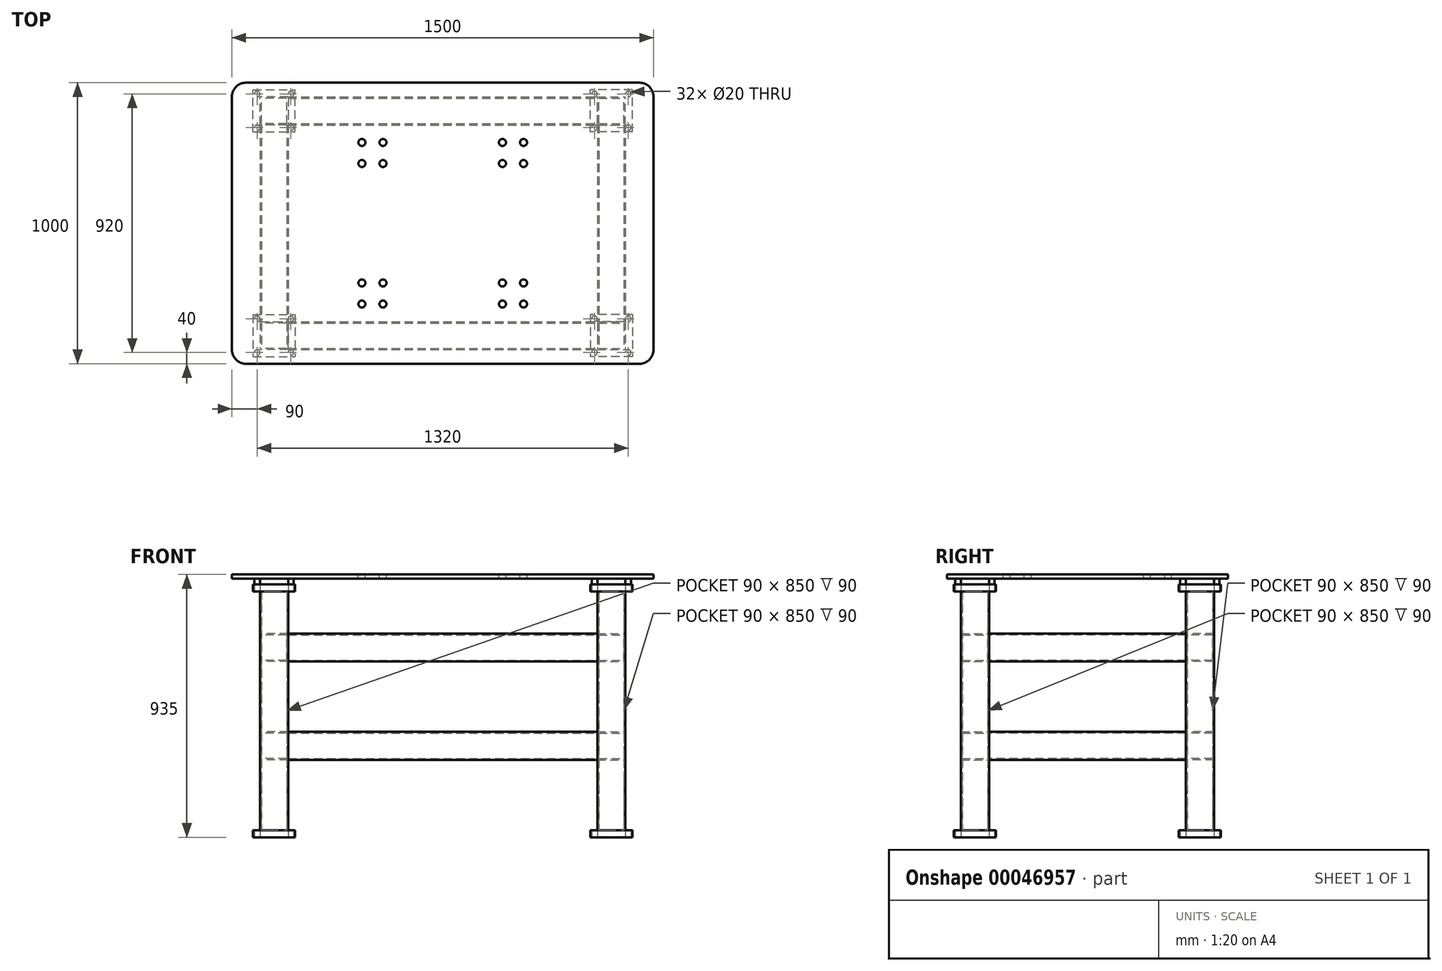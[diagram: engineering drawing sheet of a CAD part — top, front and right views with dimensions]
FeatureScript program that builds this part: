
annotation { "Feature Type Name" : "Feature", "Feature Type Description" : "" }
export const myFeature = defineFeature(function(context is Context, id is Id, definition is map)
    precondition{}
    {
        {
            var Q0;
            Q0=qCreatedBy(makeId("Top.planeOp"),FACE);
            var sketch = newSketch(context, id + "F0", { "sketchPlane" : qUnion([Q0])});
            skLineSegment(sketch, "E0.rect.bottom", {"start": v(-600, -400) * mm, "end": v(600, -400) * mm, "construction": true});
            skLineSegment(sketch, "E0.rect.top", {"start": v(-600, 400) * mm, "end": v(600, 400) * mm, "construction": true});
            skLineSegment(sketch, "E0.rect.left", {"start": v(-600, -400) * mm, "end": v(-600, 400) * mm, "construction": true});
            skLineSegment(sketch, "E0.rect.right", {"start": v(600, -400) * mm, "end": v(600, 400) * mm, "construction": true});
            skPoint(sketch, "E0.rect.middle", {"position": v(0, 0) * mm});
            skLineSegment(sketch, "E1.rect.bottom", {"start": v(-675, 325) * mm, "end": v(-525, 325) * mm});
            skLineSegment(sketch, "E1.rect.top", {"start": v(-675, 475) * mm, "end": v(-525, 475) * mm});
            skLineSegment(sketch, "E1.rect.left", {"start": v(-675, 325) * mm, "end": v(-675, 475) * mm});
            skLineSegment(sketch, "E1.rect.right", {"start": v(-525, 325) * mm, "end": v(-525, 475) * mm});
            skPoint(sketch, "E1.rect.middle", {"position": v(-600, 400) * mm});
            skLineSegment(sketch, "E2.rect.bottom", {"start": v(-660, 340) * mm, "end": v(-540, 340) * mm, "construction": true});
            skLineSegment(sketch, "E2.rect.top", {"start": v(-660, 460) * mm, "end": v(-540, 460) * mm, "construction": true});
            skLineSegment(sketch, "E2.rect.left", {"start": v(-660, 340) * mm, "end": v(-660, 460) * mm, "construction": true});
            skLineSegment(sketch, "E2.rect.right", {"start": v(-540, 340) * mm, "end": v(-540, 460) * mm, "construction": true});
            skCircle(sketch, "E3", {"center": v(-660, 460) * mm, "radius": 10 * mm});
            skCircle(sketch, "E4", {"center": v(-540, 460) * mm, "radius": 10 * mm});
            skCircle(sketch, "E5", {"center": v(-660, 340) * mm, "radius": 10 * mm});
            skCircle(sketch, "E6", {"center": v(-540, 340) * mm, "radius": 10 * mm});
            skCircle(sketch, "E7.MirrorC", {"center": v(540, 340) * mm, "radius": 10 * mm});
            skCircle(sketch, "E8.MirrorC", {"center": v(660, 460) * mm, "radius": 10 * mm});
            skCircle(sketch, "E9.MirrorC", {"center": v(660, 340) * mm, "radius": 10 * mm});
            skCircle(sketch, "E10.MirrorC", {"center": v(540, 460) * mm, "radius": 10 * mm});
            skPoint(sketch, "E11.MirrorP", {"position": v(600, 400) * mm});
            skLineSegment(sketch, "E12.MirrorCS", {"start": v(540, 340) * mm, "end": v(540, 460) * mm, "construction": true});
            skLineSegment(sketch, "E13.MirrorCS", {"start": v(660, 340) * mm, "end": v(660, 460) * mm, "construction": true});
            skLineSegment(sketch, "E14.MirrorCS", {"start": v(660, 460) * mm, "end": v(540, 460) * mm, "construction": true});
            skLineSegment(sketch, "E15.MirrorCS", {"start": v(675, 325) * mm, "end": v(525, 325) * mm});
            skLineSegment(sketch, "E16.MirrorCS", {"start": v(675, 475) * mm, "end": v(525, 475) * mm});
            skLineSegment(sketch, "E17.MirrorCS", {"start": v(675, 325) * mm, "end": v(675, 475) * mm});
            skLineSegment(sketch, "E18.MirrorCS", {"start": v(525, 325) * mm, "end": v(525, 475) * mm});
            skLineSegment(sketch, "E19.MirrorCS", {"start": v(660, 340) * mm, "end": v(540, 340) * mm, "construction": true});
            skCircle(sketch, "E20.MirrorC", {"center": v(540, -340) * mm, "radius": 10 * mm});
            skCircle(sketch, "E21.MirrorC", {"center": v(660, -340) * mm, "radius": 10 * mm});
            skCircle(sketch, "E22.MirrorC", {"center": v(-660, -460) * mm, "radius": 10 * mm});
            skCircle(sketch, "E23.MirrorC", {"center": v(-540, -340) * mm, "radius": 10 * mm});
            skCircle(sketch, "E24.MirrorC", {"center": v(-660, -340) * mm, "radius": 10 * mm});
            skCircle(sketch, "E25.MirrorC", {"center": v(-540, -460) * mm, "radius": 10 * mm});
            skCircle(sketch, "E26.MirrorC", {"center": v(660, -460) * mm, "radius": 10 * mm});
            skCircle(sketch, "E27.MirrorC", {"center": v(540, -460) * mm, "radius": 10 * mm});
            skPoint(sketch, "E28.MirrorP", {"position": v(600, -400) * mm});
            skPoint(sketch, "E29.MirrorP", {"position": v(-600, -400) * mm});
            skLineSegment(sketch, "E30.MirrorCS", {"start": v(540, -340) * mm, "end": v(540, -460) * mm, "construction": true});
            skLineSegment(sketch, "E31.MirrorCS", {"start": v(660, -460) * mm, "end": v(540, -460) * mm, "construction": true});
            skLineSegment(sketch, "E32.MirrorCS", {"start": v(675, -325) * mm, "end": v(525, -325) * mm});
            skLineSegment(sketch, "E33.MirrorCS", {"start": v(675, -325) * mm, "end": v(675, -475) * mm});
            skLineSegment(sketch, "E34.MirrorCS", {"start": v(660, -340) * mm, "end": v(540, -340) * mm, "construction": true});
            skLineSegment(sketch, "E35.MirrorCS", {"start": v(-540, -340) * mm, "end": v(-540, -460) * mm, "construction": true});
            skLineSegment(sketch, "E36.MirrorCS", {"start": v(-660, -340) * mm, "end": v(-660, -460) * mm, "construction": true});
            skLineSegment(sketch, "E37.MirrorCS", {"start": v(-660, -460) * mm, "end": v(-540, -460) * mm, "construction": true});
            skLineSegment(sketch, "E38.MirrorCS", {"start": v(-660, -340) * mm, "end": v(-540, -340) * mm, "construction": true});
            skLineSegment(sketch, "E39.MirrorCS", {"start": v(-525, -325) * mm, "end": v(-525, -475) * mm});
            skLineSegment(sketch, "E40.MirrorCS", {"start": v(-675, -325) * mm, "end": v(-675, -475) * mm});
            skLineSegment(sketch, "E41.MirrorCS", {"start": v(-675, -475) * mm, "end": v(-525, -475) * mm});
            skLineSegment(sketch, "E42.MirrorCS", {"start": v(-600, -400) * mm, "end": v(600, -400) * mm});
            skLineSegment(sketch, "E43.MirrorCS", {"start": v(525, -325) * mm, "end": v(525, -475) * mm});
            skLineSegment(sketch, "E44.MirrorCS", {"start": v(-675, -325) * mm, "end": v(-525, -325) * mm});
            skLineSegment(sketch, "E45.MirrorCS", {"start": v(660, -340) * mm, "end": v(660, -460) * mm, "construction": true});
            skLineSegment(sketch, "E46.MirrorCS", {"start": v(675, -475) * mm, "end": v(525, -475) * mm});
            skSolve(sketch);
        }
        {
            var Q0;
            Q0=qSketchRegion(id+"F0",true);
            extrude(context, id + "F1", {"entities" : qUnion([Q0]), "depth" : 25 * mm});
        }
        {
            var Q0;
            Q0=makeQuery(id+"F1.opExtrude","CAP_FACE",FACE,{"disambiguationData":[OSD([sQuery(id+"F0.wireOp",EDGE,"E1.rect.bottom"),sQuery(id+"F0.wireOp",EDGE,"E1.rect.top"),sQuery(id+"F0.wireOp",EDGE,"E1.rect.left"),sQuery(id+"F0.wireOp",EDGE,"E1.rect.right"),sQuery(id+"F0.wireOp",EDGE,"E3"),sQuery(id+"F0.wireOp",EDGE,"E4"),sQuery(id+"F0.wireOp",EDGE,"E5"),sQuery(id+"F0.wireOp",EDGE,"E6")])],"isStart":false});
            var sketch = newSketch(context, id + "F2", { "sketchPlane" : qUnion([Q0])});
            skLineSegment(sketch, "E47.rect.bottom", {"start": v(-550, 350) * mm, "end": v(-650, 350) * mm});
            skLineSegment(sketch, "E47.rect.top", {"start": v(-550, 450) * mm, "end": v(-650, 450) * mm});
            skLineSegment(sketch, "E47.rect.left", {"start": v(-550, 350) * mm, "end": v(-550, 450) * mm});
            skLineSegment(sketch, "E47.rect.right", {"start": v(-650, 350) * mm, "end": v(-650, 450) * mm});
            skPoint(sketch, "E47.rect.middle", {"position": v(-600, 400) * mm});
            skPoint(sketch, "E47.rect.middle.positionSnap0", {"position": v(-675, 400) * mm});
            skPoint(sketch, "E47.rect.centerSnap0", {"position": v(-675, 400) * mm});
            skLineSegment(sketch, "E48.rect.bottom", {"start": v(-555, 355) * mm, "end": v(-645, 355) * mm});
            skLineSegment(sketch, "E48.rect.top", {"start": v(-555, 445) * mm, "end": v(-645, 445) * mm});
            skLineSegment(sketch, "E48.rect.left", {"start": v(-555, 355) * mm, "end": v(-555, 445) * mm});
            skLineSegment(sketch, "E48.rect.right", {"start": v(-645, 355) * mm, "end": v(-645, 445) * mm});
            skPoint(sketch, "E49.MirrorP", {"position": v(600, 400) * mm});
            skPoint(sketch, "E50.MirrorP", {"position": v(675, 400) * mm});
            skLineSegment(sketch, "E51.MirrorCS", {"start": v(645, 355) * mm, "end": v(645, 445) * mm});
            skLineSegment(sketch, "E52.MirrorCS", {"start": v(555, 355) * mm, "end": v(555, 445) * mm});
            skLineSegment(sketch, "E53.MirrorCS", {"start": v(555, 445) * mm, "end": v(645, 445) * mm});
            skLineSegment(sketch, "E54.MirrorCS", {"start": v(555, 355) * mm, "end": v(645, 355) * mm});
            skLineSegment(sketch, "E55.MirrorCS", {"start": v(650, 350) * mm, "end": v(650, 450) * mm});
            skLineSegment(sketch, "E56.MirrorCS", {"start": v(550, 350) * mm, "end": v(650, 350) * mm});
            skLineSegment(sketch, "E57.MirrorCS", {"start": v(550, 350) * mm, "end": v(550, 450) * mm});
            skLineSegment(sketch, "E58.MirrorCS", {"start": v(550, 450) * mm, "end": v(650, 450) * mm});
            skLineSegment(sketch, "E59.MirrorCS", {"start": v(650, -350) * mm, "end": v(650, -450) * mm});
            skPoint(sketch, "E60.MirrorP", {"position": v(-675, -400) * mm});
            skPoint(sketch, "E61.MirrorP", {"position": v(600, -400) * mm});
            skPoint(sketch, "E62.MirrorP", {"position": v(-600, -400) * mm});
            skPoint(sketch, "E63.MirrorP", {"position": v(675, -400) * mm});
            skLineSegment(sketch, "E64.MirrorCS", {"start": v(-555, -355) * mm, "end": v(-555, -445) * mm});
            skLineSegment(sketch, "E65.MirrorCS", {"start": v(-555, -445) * mm, "end": v(-645, -445) * mm});
            skLineSegment(sketch, "E66.MirrorCS", {"start": v(-555, -355) * mm, "end": v(-645, -355) * mm});
            skLineSegment(sketch, "E67.MirrorCS", {"start": v(-650, -350) * mm, "end": v(-650, -450) * mm});
            skLineSegment(sketch, "E68.MirrorCS", {"start": v(-550, -350) * mm, "end": v(-550, -450) * mm});
            skLineSegment(sketch, "E69.MirrorCS", {"start": v(-550, -450) * mm, "end": v(-650, -450) * mm});
            skLineSegment(sketch, "E70.MirrorCS", {"start": v(-550, -350) * mm, "end": v(-650, -350) * mm});
            skLineSegment(sketch, "E71.MirrorCS", {"start": v(550, -450) * mm, "end": v(650, -450) * mm});
            skLineSegment(sketch, "E72.MirrorCS", {"start": v(550, -350) * mm, "end": v(550, -450) * mm});
            skLineSegment(sketch, "E73.MirrorCS", {"start": v(550, -350) * mm, "end": v(650, -350) * mm});
            skLineSegment(sketch, "E74.MirrorCS", {"start": v(-645, -355) * mm, "end": v(-645, -445) * mm});
            skLineSegment(sketch, "E75.MirrorCS", {"start": v(645, -355) * mm, "end": v(645, -445) * mm});
            skLineSegment(sketch, "E76.MirrorCS", {"start": v(555, -355) * mm, "end": v(555, -445) * mm});
            skLineSegment(sketch, "E77.MirrorCS", {"start": v(555, -355) * mm, "end": v(645, -355) * mm});
            skLineSegment(sketch, "E78.MirrorCS", {"start": v(555, -445) * mm, "end": v(645, -445) * mm});
            skSolve(sketch);
        }
        {
            var Q0;
            Q0=qSketchRegion(id+"F2",true);
            extrude(context, id + "F3", {"entities" : qUnion([Q0]), "operationType" : NewBodyOperationType.ADD, "depth" : 850 * mm});
        }
        {
            var Q0;
            Q0=makeQuery(id+"F3.opExtrude","CAP_FACE",FACE,{"disambiguationData":[OSD([sQuery(id+"F2.wireOp",EDGE,"E47.rect.bottom"),sQuery(id+"F2.wireOp",EDGE,"E47.rect.top"),sQuery(id+"F2.wireOp",EDGE,"E47.rect.left"),sQuery(id+"F2.wireOp",EDGE,"E47.rect.right"),sQuery(id+"F2.wireOp",EDGE,"E48.rect.bottom"),sQuery(id+"F2.wireOp",EDGE,"E48.rect.top"),sQuery(id+"F2.wireOp",EDGE,"E48.rect.left"),sQuery(id+"F2.wireOp",EDGE,"E48.rect.right")])],"isStart":false});
            var sketch = newSketch(context, id + "F4", { "sketchPlane" : qUnion([Q0])});
            skLineSegment(sketch, "E79.rect.bottom", {"start": v(-600, -400) * mm, "end": v(600, -400) * mm, "construction": true});
            skLineSegment(sketch, "E79.rect.top", {"start": v(-600, 400) * mm, "end": v(600, 400) * mm, "construction": true});
            skLineSegment(sketch, "E79.rect.left", {"start": v(-600, -400) * mm, "end": v(-600, 400) * mm, "construction": true});
            skLineSegment(sketch, "E79.rect.right", {"start": v(600, -400) * mm, "end": v(600, 400) * mm, "construction": true});
            skLineSegment(sketch, "E80.rect.bottom", {"start": v(-675, 325) * mm, "end": v(-525, 325) * mm});
            skLineSegment(sketch, "E80.rect.top", {"start": v(-675, 475) * mm, "end": v(-525, 475) * mm});
            skLineSegment(sketch, "E80.rect.left", {"start": v(-675, 325) * mm, "end": v(-675, 475) * mm});
            skLineSegment(sketch, "E80.rect.right", {"start": v(-525, 325) * mm, "end": v(-525, 475) * mm});
            skPoint(sketch, "E80.rect.middle", {"position": v(-600, 400) * mm});
            skLineSegment(sketch, "E81.rect.bottom", {"start": v(-660, 340) * mm, "end": v(-540, 340) * mm, "construction": true});
            skLineSegment(sketch, "E81.rect.top", {"start": v(-660, 460) * mm, "end": v(-540, 460) * mm, "construction": true});
            skLineSegment(sketch, "E81.rect.left", {"start": v(-660, 340) * mm, "end": v(-660, 460) * mm, "construction": true});
            skLineSegment(sketch, "E81.rect.right", {"start": v(-540, 340) * mm, "end": v(-540, 460) * mm, "construction": true});
            skCircle(sketch, "E82", {"center": v(-660, 460) * mm, "radius": 10 * mm});
            skCircle(sketch, "E83", {"center": v(-540, 460) * mm, "radius": 10 * mm});
            skCircle(sketch, "E84", {"center": v(-660, 340) * mm, "radius": 10 * mm});
            skCircle(sketch, "E85", {"center": v(-540, 340) * mm, "radius": 10 * mm});
            skPoint(sketch, "E86.MirrorP", {"position": v(600, 400) * mm});
            skPoint(sketch, "E87.MirrorP", {"position": v(-1214.7, -400) * mm});
            skLineSegment(sketch, "E88.MirrorCS", {"start": v(-1214.7, -400) * mm, "end": v(-14.7, -400) * mm});
            skCircle(sketch, "E89.MirrorC", {"center": v(540, 340) * mm, "radius": 10 * mm});
            skCircle(sketch, "E90.MirrorC", {"center": v(660, 460) * mm, "radius": 10 * mm});
            skCircle(sketch, "E91.MirrorC", {"center": v(660, 340) * mm, "radius": 10 * mm});
            skCircle(sketch, "E92.MirrorC", {"center": v(540, 460) * mm, "radius": 10 * mm});
            skLineSegment(sketch, "E93.MirrorCS", {"start": v(660, 340) * mm, "end": v(540, 340) * mm, "construction": true});
            skLineSegment(sketch, "E94.MirrorCS", {"start": v(525, 325) * mm, "end": v(525, 475) * mm});
            skLineSegment(sketch, "E95.MirrorCS", {"start": v(675, 325) * mm, "end": v(675, 475) * mm});
            skLineSegment(sketch, "E96.MirrorCS", {"start": v(540, 340) * mm, "end": v(540, 460) * mm, "construction": true});
            skLineSegment(sketch, "E97.MirrorCS", {"start": v(675, 475) * mm, "end": v(525, 475) * mm});
            skLineSegment(sketch, "E98.MirrorCS", {"start": v(660, 340) * mm, "end": v(660, 460) * mm, "construction": true});
            skLineSegment(sketch, "E99.MirrorCS", {"start": v(660, 460) * mm, "end": v(540, 460) * mm, "construction": true});
            skLineSegment(sketch, "E100.MirrorCS", {"start": v(675, 325) * mm, "end": v(525, 325) * mm});
            skCircle(sketch, "E101.MirrorC", {"center": v(-660, -460) * mm, "radius": 10 * mm});
            skPoint(sketch, "E102.MirrorP", {"position": v(600, -400) * mm});
            skCircle(sketch, "E103.MirrorC", {"center": v(660, -460) * mm, "radius": 10 * mm});
            skCircle(sketch, "E104.MirrorC", {"center": v(-540, -340) * mm, "radius": 10 * mm});
            skCircle(sketch, "E105.MirrorC", {"center": v(-660, -340) * mm, "radius": 10 * mm});
            skCircle(sketch, "E106.MirrorC", {"center": v(660, -340) * mm, "radius": 10 * mm});
            skCircle(sketch, "E107.MirrorC", {"center": v(540, -460) * mm, "radius": 10 * mm});
            skCircle(sketch, "E108.MirrorC", {"center": v(-540, -460) * mm, "radius": 10 * mm});
            skCircle(sketch, "E109.MirrorC", {"center": v(540, -340) * mm, "radius": 10 * mm});
            skPoint(sketch, "E110.MirrorP", {"position": v(-600, -400) * mm});
            skLineSegment(sketch, "E111.MirrorCS", {"start": v(660, -340) * mm, "end": v(540, -340) * mm, "construction": true});
            skLineSegment(sketch, "E112.MirrorCS", {"start": v(-540, -340) * mm, "end": v(-540, -460) * mm, "construction": true});
            skLineSegment(sketch, "E113.MirrorCS", {"start": v(660, -460) * mm, "end": v(540, -460) * mm, "construction": true});
            skLineSegment(sketch, "E114.MirrorCS", {"start": v(675, -325) * mm, "end": v(525, -325) * mm});
            skLineSegment(sketch, "E115.MirrorCS", {"start": v(-660, -340) * mm, "end": v(-660, -460) * mm, "construction": true});
            skLineSegment(sketch, "E116.MirrorCS", {"start": v(-660, -460) * mm, "end": v(-540, -460) * mm, "construction": true});
            skLineSegment(sketch, "E117.MirrorCS", {"start": v(540, -340) * mm, "end": v(540, -460) * mm, "construction": true});
            skLineSegment(sketch, "E118.MirrorCS", {"start": v(-660, -340) * mm, "end": v(-540, -340) * mm, "construction": true});
            skLineSegment(sketch, "E119.MirrorCS", {"start": v(-525, -325) * mm, "end": v(-525, -475) * mm});
            skLineSegment(sketch, "E120.MirrorCS", {"start": v(675, -475) * mm, "end": v(525, -475) * mm});
            skLineSegment(sketch, "E121.MirrorCS", {"start": v(525, -325) * mm, "end": v(525, -475) * mm});
            skLineSegment(sketch, "E122.MirrorCS", {"start": v(-675, -475) * mm, "end": v(-525, -475) * mm});
            skLineSegment(sketch, "E123.MirrorCS", {"start": v(660, -340) * mm, "end": v(660, -460) * mm, "construction": true});
            skLineSegment(sketch, "E124.MirrorCS", {"start": v(-675, -325) * mm, "end": v(-675, -475) * mm});
            skLineSegment(sketch, "E125.MirrorCS", {"start": v(-600, -400) * mm, "end": v(600, -400) * mm});
            skLineSegment(sketch, "E126.MirrorCS", {"start": v(675, -325) * mm, "end": v(675, -475) * mm});
            skLineSegment(sketch, "E127.MirrorCS", {"start": v(-675, -325) * mm, "end": v(-525, -325) * mm});
            skSolve(sketch);
        }
        {
            var Q0;
            Q0=qSketchRegion(id+"F4",true);
            extrude(context, id + "F5", {"entities" : qUnion([Q0]), "operationType" : NewBodyOperationType.ADD, "depth" : 25 * mm});
        }
        {
            var Q0;
            Q0=makeQuery(id+"F3.opExtrude","SWEPT_FACE",FACE,{"disambiguationData":[OSD([sQuery(id+"F2.wireOp",EDGE,"E72.MirrorCS")])]});
            var sketch = newSketch(context, id + "F6", { "sketchPlane" : qUnion([Q0])});
            skLineSegment(sketch, "E128", {"start": v(350, 875) * mm, "end": v(350, 725) * mm, "construction": true});
            skLineSegment(sketch, "E129", {"start": v(350, 25) * mm, "end": v(350, 275) * mm, "construction": true});
            skLineSegment(sketch, "E130.bottom", {"start": v(350, 725) * mm, "end": v(450, 725) * mm});
            skLineSegment(sketch, "E130.top", {"start": v(350, 625) * mm, "end": v(450, 625) * mm});
            skLineSegment(sketch, "E130.left", {"start": v(350, 725) * mm, "end": v(350, 625) * mm});
            skLineSegment(sketch, "E130.right", {"start": v(450, 725) * mm, "end": v(450, 625) * mm});
            skLineSegment(sketch, "E131.bottom", {"start": v(355, 720) * mm, "end": v(445, 720) * mm});
            skLineSegment(sketch, "E131.top", {"start": v(355, 630) * mm, "end": v(445, 630) * mm});
            skLineSegment(sketch, "E131.left", {"start": v(355, 720) * mm, "end": v(355, 630) * mm});
            skLineSegment(sketch, "E131.right", {"start": v(445, 720) * mm, "end": v(445, 630) * mm});
            skLineSegment(sketch, "E132.bottom", {"start": v(350, 275) * mm, "end": v(450, 275) * mm});
            skLineSegment(sketch, "E132.top", {"start": v(350, 375) * mm, "end": v(450, 375) * mm});
            skLineSegment(sketch, "E132.left", {"start": v(350, 275) * mm, "end": v(350, 375) * mm});
            skLineSegment(sketch, "E132.right", {"start": v(450, 275) * mm, "end": v(450, 375) * mm});
            skLineSegment(sketch, "E133.bottom", {"start": v(355, 280) * mm, "end": v(445, 280) * mm});
            skLineSegment(sketch, "E133.top", {"start": v(355, 370) * mm, "end": v(445, 370) * mm});
            skLineSegment(sketch, "E133.left", {"start": v(355, 280) * mm, "end": v(355, 370) * mm});
            skLineSegment(sketch, "E133.right", {"start": v(445, 280) * mm, "end": v(445, 370) * mm});
            skLineSegment(sketch, "E134.MirrorCS", {"start": v(-350, 725) * mm, "end": v(-450, 725) * mm});
            skLineSegment(sketch, "E135.MirrorCS", {"start": v(-355, 720) * mm, "end": v(-445, 720) * mm});
            skLineSegment(sketch, "E136.MirrorCS", {"start": v(-450, 725) * mm, "end": v(-450, 625) * mm});
            skLineSegment(sketch, "E137.MirrorCS", {"start": v(-445, 720) * mm, "end": v(-445, 630) * mm});
            skLineSegment(sketch, "E138.MirrorCS", {"start": v(-355, 720) * mm, "end": v(-355, 630) * mm});
            skLineSegment(sketch, "E139.MirrorCS", {"start": v(-350, 725) * mm, "end": v(-350, 625) * mm});
            skLineSegment(sketch, "E140.MirrorCS", {"start": v(-355, 630) * mm, "end": v(-445, 630) * mm});
            skLineSegment(sketch, "E141.MirrorCS", {"start": v(-350, 625) * mm, "end": v(-450, 625) * mm});
            skLineSegment(sketch, "E142.MirrorCS", {"start": v(-350, 375) * mm, "end": v(-450, 375) * mm});
            skLineSegment(sketch, "E143.MirrorCS", {"start": v(-355, 370) * mm, "end": v(-445, 370) * mm});
            skLineSegment(sketch, "E144.MirrorCS", {"start": v(-450, 275) * mm, "end": v(-450, 375) * mm});
            skLineSegment(sketch, "E145.MirrorCS", {"start": v(-445, 280) * mm, "end": v(-445, 370) * mm});
            skLineSegment(sketch, "E146.MirrorCS", {"start": v(-355, 280) * mm, "end": v(-355, 370) * mm});
            skLineSegment(sketch, "E147.MirrorCS", {"start": v(-350, 275) * mm, "end": v(-350, 375) * mm});
            skLineSegment(sketch, "E148.MirrorCS", {"start": v(-355, 280) * mm, "end": v(-445, 280) * mm});
            skLineSegment(sketch, "E149.MirrorCS", {"start": v(-350, 275) * mm, "end": v(-450, 275) * mm});
            skSolve(sketch);
        }
        {
            var Q0;
            Q0=qSketchRegion(id+"F6",true);
            var Q1;
            Q1=makeQuery(id+"F3.opExtrude","SWEPT_FACE",FACE,{"disambiguationData":[OSD([sQuery(id+"F2.wireOp",EDGE,"E68.MirrorCS")])]});
            extrude(context, id + "F7", {"entities" : qUnion([Q0]), "endBound" : BoundingType.UP_TO_SURFACE, "endBoundEntityFace" : qUnion([Q1]), "depth" : 25 * mm});
        }
        {
            var Q0;
            Q0=makeQuery(id+"F3.opExtrude","SWEPT_FACE",FACE,{"disambiguationData":[OSD([sQuery(id+"F2.wireOp",EDGE,"E73.MirrorCS")])]});
            var sketch = newSketch(context, id + "F8", { "sketchPlane" : qUnion([Q0])});
            skLineSegment(sketch, "E150", {"start": v(-650, 875) * mm, "end": v(-650, 725) * mm, "construction": true});
            skLineSegment(sketch, "E151", {"start": v(-650, 25) * mm, "end": v(-650, 275) * mm, "construction": true});
            skLineSegment(sketch, "E152.bottom", {"start": v(-650, 725) * mm, "end": v(-550, 725) * mm});
            skLineSegment(sketch, "E152.top", {"start": v(-650, 625) * mm, "end": v(-550, 625) * mm});
            skLineSegment(sketch, "E152.left", {"start": v(-650, 725) * mm, "end": v(-650, 625) * mm});
            skLineSegment(sketch, "E152.right", {"start": v(-550, 725) * mm, "end": v(-550, 625) * mm});
            skLineSegment(sketch, "E153.bottom", {"start": v(-645, 720) * mm, "end": v(-555, 720) * mm});
            skLineSegment(sketch, "E153.top", {"start": v(-645, 630) * mm, "end": v(-555, 630) * mm});
            skLineSegment(sketch, "E153.left", {"start": v(-645, 720) * mm, "end": v(-645, 630) * mm});
            skLineSegment(sketch, "E153.right", {"start": v(-555, 720) * mm, "end": v(-555, 630) * mm});
            skLineSegment(sketch, "E154.bottom", {"start": v(-650, 275) * mm, "end": v(-550, 275) * mm});
            skLineSegment(sketch, "E154.top", {"start": v(-650, 375) * mm, "end": v(-550, 375) * mm});
            skLineSegment(sketch, "E154.left", {"start": v(-650, 275) * mm, "end": v(-650, 375) * mm});
            skLineSegment(sketch, "E154.right", {"start": v(-550, 275) * mm, "end": v(-550, 375) * mm});
            skLineSegment(sketch, "E155.bottom", {"start": v(-645, 280) * mm, "end": v(-555, 280) * mm});
            skLineSegment(sketch, "E155.top", {"start": v(-645, 370) * mm, "end": v(-555, 370) * mm});
            skLineSegment(sketch, "E155.left", {"start": v(-645, 280) * mm, "end": v(-645, 370) * mm});
            skLineSegment(sketch, "E155.right", {"start": v(-555, 280) * mm, "end": v(-555, 370) * mm});
            skLineSegment(sketch, "E156.MirrorCS", {"start": v(650, 875) * mm, "end": v(650, 725) * mm});
            skLineSegment(sketch, "E157.MirrorCS", {"start": v(650, 725) * mm, "end": v(550, 725) * mm});
            skLineSegment(sketch, "E158.MirrorCS", {"start": v(645, 720) * mm, "end": v(555, 720) * mm});
            skLineSegment(sketch, "E159.MirrorCS", {"start": v(550, 725) * mm, "end": v(550, 625) * mm});
            skLineSegment(sketch, "E160.MirrorCS", {"start": v(555, 720) * mm, "end": v(555, 630) * mm});
            skLineSegment(sketch, "E161.MirrorCS", {"start": v(645, 720) * mm, "end": v(645, 630) * mm});
            skLineSegment(sketch, "E162.MirrorCS", {"start": v(650, 725) * mm, "end": v(650, 625) * mm});
            skLineSegment(sketch, "E163.MirrorCS", {"start": v(645, 630) * mm, "end": v(555, 630) * mm});
            skLineSegment(sketch, "E164.MirrorCS", {"start": v(650, 625) * mm, "end": v(550, 625) * mm});
            skLineSegment(sketch, "E165.MirrorCS", {"start": v(650, 375) * mm, "end": v(550, 375) * mm});
            skLineSegment(sketch, "E166.MirrorCS", {"start": v(645, 370) * mm, "end": v(555, 370) * mm});
            skLineSegment(sketch, "E167.MirrorCS", {"start": v(550, 275) * mm, "end": v(550, 375) * mm});
            skLineSegment(sketch, "E168.MirrorCS", {"start": v(555, 280) * mm, "end": v(555, 370) * mm});
            skLineSegment(sketch, "E169.MirrorCS", {"start": v(645, 280) * mm, "end": v(645, 370) * mm});
            skLineSegment(sketch, "E170.MirrorCS", {"start": v(650, 275) * mm, "end": v(650, 375) * mm});
            skLineSegment(sketch, "E171.MirrorCS", {"start": v(645, 280) * mm, "end": v(555, 280) * mm});
            skLineSegment(sketch, "E172.MirrorCS", {"start": v(650, 275) * mm, "end": v(550, 275) * mm});
            skSolve(sketch);
        }
        {
            var Q0;
            Q0=qSketchRegion(id+"F8",true);
            var Q1;
            Q1=makeQuery(id+"F3.opExtrude","SWEPT_FACE",FACE,{"disambiguationData":[OSD([sQuery(id+"F2.wireOp",EDGE,"E47.rect.bottom")])]});
            extrude(context, id + "F9", {"entities" : qUnion([Q0]), "endBound" : BoundingType.UP_TO_SURFACE, "endBoundEntityFace" : qUnion([Q1]), "depth" : 25 * mm});
        }
        {
            var Q0;
            Q0=makeQuery(id+"F5.opExtrude","CAP_FACE",FACE,{"disambiguationData":[OSD([sQuery(id+"F4.wireOp",EDGE,"E80.rect.bottom"),sQuery(id+"F4.wireOp",EDGE,"E80.rect.top"),sQuery(id+"F4.wireOp",EDGE,"E80.rect.left"),sQuery(id+"F4.wireOp",EDGE,"E80.rect.right"),sQuery(id+"F4.wireOp",EDGE,"E82"),sQuery(id+"F4.wireOp",EDGE,"E83"),sQuery(id+"F4.wireOp",EDGE,"E84"),sQuery(id+"F4.wireOp",EDGE,"E85")])],"isStart":false});
            var sketch = newSketch(context, id + "F10", { "sketchPlane" : qUnion([Q0])});
            skLineSegment(sketch, "E173.rect.bottom", {"start": v(-750, 500) * mm, "end": v(750, 500) * mm});
            skLineSegment(sketch, "E173.rect.top", {"start": v(-750, -500) * mm, "end": v(750, -500) * mm});
            skLineSegment(sketch, "E173.rect.left", {"start": v(-750, 500) * mm, "end": v(-750, -500) * mm});
            skLineSegment(sketch, "E173.rect.right", {"start": v(750, 500) * mm, "end": v(750, -500) * mm});
            skPoint(sketch, "E173.rect.middle", {"position": v(0, 0) * mm});
            skSolve(sketch);
        }
        {
            var Q0;
            Q0=qSketchRegion(id+"F10",true);
            extrude(context, id + "F11", {"entities" : qUnion([Q0]), "depth" : 35 * mm});
        }
        {
            var Q0;
            Q0=makeQuery(id+"F11.opExtrude","CAP_FACE",FACE,{"disambiguationData":[OSD([sQuery(id+"F10.wireOp",EDGE,"E173.rect.bottom"),sQuery(id+"F10.wireOp",EDGE,"E173.rect.top"),sQuery(id+"F10.wireOp",EDGE,"E173.rect.left"),sQuery(id+"F10.wireOp",EDGE,"E173.rect.right")])],"isStart":true});
            var sketch = newSketch(context, id + "F12", { "sketchPlane" : qUnion([Q0])});
            skCircle(sketch, "E174.0", {"center": v(-660, 460) * mm, "radius": 10 * mm});
            skCircle(sketch, "E174.1", {"center": v(-540, 460) * mm, "radius": 10 * mm});
            skCircle(sketch, "E174.2", {"center": v(-660, 340) * mm, "radius": 10 * mm});
            skCircle(sketch, "E174.3", {"center": v(-540, 340) * mm, "radius": 10 * mm});
            skCircle(sketch, "E175.0", {"center": v(-660, -460) * mm, "radius": 10 * mm});
            skCircle(sketch, "E175.1", {"center": v(-660, -340) * mm, "radius": 10 * mm});
            skCircle(sketch, "E175.2", {"center": v(-540, -340) * mm, "radius": 10 * mm});
            skCircle(sketch, "E175.3", {"center": v(-540, -460) * mm, "radius": 10 * mm});
            skCircle(sketch, "E175.4", {"center": v(540, -340) * mm, "radius": 10 * mm});
            skCircle(sketch, "E175.5", {"center": v(660, -340) * mm, "radius": 10 * mm});
            skCircle(sketch, "E175.6", {"center": v(540, -460) * mm, "radius": 10 * mm});
            skCircle(sketch, "E175.7", {"center": v(660, -460) * mm, "radius": 10 * mm});
            skCircle(sketch, "E175.8", {"center": v(540, 460) * mm, "radius": 10 * mm});
            skCircle(sketch, "E175.9", {"center": v(660, 460) * mm, "radius": 10 * mm});
            skCircle(sketch, "E175.10", {"center": v(540, 340) * mm, "radius": 10 * mm});
            skCircle(sketch, "E175.11", {"center": v(660, 340) * mm, "radius": 10 * mm});
            skSolve(sketch);
        }
        {
            var Q0;
            Q0=makeQuery(id+"F12.imprint","IMPRINT",FACE,{"disambiguationData":[TD([[makeQuery(id+"F12.imprint","IMPRINT",EDGE,{"derivedFrom":sQuery(id+"F12.wireOp",EDGE,"E175.0")}),-1.0]])]});
            var Q1;
            Q1=makeQuery(id+"F12.imprint","IMPRINT",FACE,{"disambiguationData":[TD([[makeQuery(id+"F12.imprint","IMPRINT",EDGE,{"derivedFrom":sQuery(id+"F12.wireOp",EDGE,"E175.1")}),-1.0]])]});
            var Q2;
            Q2=makeQuery(id+"F12.imprint","IMPRINT",FACE,{"disambiguationData":[TD([[makeQuery(id+"F12.imprint","IMPRINT",EDGE,{"derivedFrom":sQuery(id+"F12.wireOp",EDGE,"E175.2")}),-1.0]])]});
            var Q3;
            Q3=makeQuery(id+"F12.imprint","IMPRINT",FACE,{"disambiguationData":[TD([[makeQuery(id+"F12.imprint","IMPRINT",EDGE,{"derivedFrom":sQuery(id+"F12.wireOp",EDGE,"E175.3")}),-1.0]])]});
            var Q4;
            Q4=makeQuery(id+"F12.imprint","IMPRINT",FACE,{"disambiguationData":[TD([[makeQuery(id+"F12.imprint","IMPRINT",EDGE,{"derivedFrom":sQuery(id+"F12.wireOp",EDGE,"E174.2")}),1.0]])]});
            var Q5;
            Q5=makeQuery(id+"F12.imprint","IMPRINT",FACE,{"disambiguationData":[TD([[makeQuery(id+"F12.imprint","IMPRINT",EDGE,{"derivedFrom":sQuery(id+"F12.wireOp",EDGE,"E174.0")}),1.0]])]});
            var Q6;
            Q6=makeQuery(id+"F12.imprint","IMPRINT",FACE,{"disambiguationData":[TD([[makeQuery(id+"F12.imprint","IMPRINT",EDGE,{"derivedFrom":sQuery(id+"F12.wireOp",EDGE,"E174.1")}),1.0]])]});
            var Q7;
            Q7=makeQuery(id+"F12.imprint","IMPRINT",FACE,{"disambiguationData":[TD([[makeQuery(id+"F12.imprint","IMPRINT",EDGE,{"derivedFrom":sQuery(id+"F12.wireOp",EDGE,"E174.3")}),1.0]])]});
            var Q8;
            Q8=makeQuery(id+"F12.imprint","IMPRINT",FACE,{"disambiguationData":[TD([[makeQuery(id+"F12.imprint","IMPRINT",EDGE,{"derivedFrom":sQuery(id+"F12.wireOp",EDGE,"E175.8")}),-1.0]])]});
            var Q9;
            Q9=makeQuery(id+"F12.imprint","IMPRINT",FACE,{"disambiguationData":[TD([[makeQuery(id+"F12.imprint","IMPRINT",EDGE,{"derivedFrom":sQuery(id+"F12.wireOp",EDGE,"E175.9")}),-1.0]])]});
            var Q10;
            Q10=makeQuery(id+"F12.imprint","IMPRINT",FACE,{"disambiguationData":[TD([[makeQuery(id+"F12.imprint","IMPRINT",EDGE,{"derivedFrom":sQuery(id+"F12.wireOp",EDGE,"E175.11")}),-1.0]])]});
            var Q11;
            Q11=makeQuery(id+"F12.imprint","IMPRINT",FACE,{"disambiguationData":[TD([[makeQuery(id+"F12.imprint","IMPRINT",EDGE,{"derivedFrom":sQuery(id+"F12.wireOp",EDGE,"E175.10")}),-1.0]])]});
            var Q12;
            Q12=makeQuery(id+"F12.imprint","IMPRINT",FACE,{"disambiguationData":[TD([[makeQuery(id+"F12.imprint","IMPRINT",EDGE,{"derivedFrom":sQuery(id+"F12.wireOp",EDGE,"E175.5")}),1.0]])]});
            var Q13;
            Q13=makeQuery(id+"F12.imprint","IMPRINT",FACE,{"disambiguationData":[TD([[makeQuery(id+"F12.imprint","IMPRINT",EDGE,{"derivedFrom":sQuery(id+"F12.wireOp",EDGE,"E175.4")}),1.0]])]});
            var Q14;
            Q14=makeQuery(id+"F12.imprint","IMPRINT",FACE,{"disambiguationData":[TD([[makeQuery(id+"F12.imprint","IMPRINT",EDGE,{"derivedFrom":sQuery(id+"F12.wireOp",EDGE,"E175.7")}),1.0]])]});
            var Q15;
            Q15=makeQuery(id+"F12.imprint","IMPRINT",FACE,{"disambiguationData":[TD([[makeQuery(id+"F12.imprint","IMPRINT",EDGE,{"derivedFrom":sQuery(id+"F12.wireOp",EDGE,"E175.6")}),1.0]])]});
            extrude(context, id + "F13", {"entities" : qUnion([Q0, Q1, Q2, Q3, Q4, Q5, Q6, Q7, Q8, Q9, Q10, Q11, Q12, Q13, Q14, Q15]), "operationType" : NewBodyOperationType.REMOVE, "oppositeDirection" : true, "depth" : 20 * mm});
        }
        {
            var Q0;
            Q0=makeQuery(id+"F11.opExtrude","SWEPT_EDGE",EDGE,{"disambiguationData":[OSD([sQuery(id+"F10.wireOp",EDGE,"E173.rect.bottom"),sQuery(id+"F10.wireOp",EDGE,"E173.rect.right")])]});
            var Q1;
            Q1=makeQuery(id+"F11.opExtrude","SWEPT_EDGE",EDGE,{"disambiguationData":[OSD([sQuery(id+"F10.wireOp",EDGE,"E173.rect.top"),sQuery(id+"F10.wireOp",EDGE,"E173.rect.right")])]});
            var Q2;
            Q2=makeQuery(id+"F11.opExtrude","SWEPT_EDGE",EDGE,{"disambiguationData":[OSD([sQuery(id+"F10.wireOp",EDGE,"E173.rect.bottom"),sQuery(id+"F10.wireOp",EDGE,"E173.rect.left")])]});
            var Q3;
            Q3=makeQuery(id+"F11.opExtrude","SWEPT_EDGE",EDGE,{"disambiguationData":[OSD([sQuery(id+"F10.wireOp",EDGE,"E173.rect.top"),sQuery(id+"F10.wireOp",EDGE,"E173.rect.left")])]});
            fillet(context, id + "F14", {"entities" : qUnion([Q0, Q1, Q2, Q3]), "radius" : 50 * mm, "tangentPropagation" : true, "allowEdgeOverflow" : false});
        }
        {
            var Q0;
            Q0=makeQuery(id+"F11.opExtrude","CAP_FACE",FACE,{"disambiguationData":[OSD([sQuery(id+"F10.wireOp",EDGE,"E173.rect.bottom"),sQuery(id+"F10.wireOp",EDGE,"E173.rect.top"),sQuery(id+"F10.wireOp",EDGE,"E173.rect.left"),sQuery(id+"F10.wireOp",EDGE,"E173.rect.right")])],"isStart":false});
            var sketch = newSketch(context, id + "F15", { "sketchPlane" : qUnion([Q0])});
            skLineSegment(sketch, "E176", {"start": v(0, 0) * mm, "end": v(-750, 0) * mm, "construction": true});
            skLineSegment(sketch, "E177", {"start": v(0, 0) * mm, "end": v(0, 500) * mm, "construction": true});
            skLineSegment(sketch, "E178.rect.bottom", {"start": v(-250, 250) * mm, "end": v(250, 250) * mm, "construction": true});
            skLineSegment(sketch, "E178.rect.top", {"start": v(-250, -250) * mm, "end": v(250, -250) * mm, "construction": true});
            skLineSegment(sketch, "E178.rect.left", {"start": v(-250, 250) * mm, "end": v(-250, -250) * mm, "construction": true});
            skLineSegment(sketch, "E178.rect.right", {"start": v(250, 250) * mm, "end": v(250, -250) * mm, "construction": true});
            skPoint(sketch, "E178.rect.middle", {"position": v(0, 0) * mm});
            skLineSegment(sketch, "E179.rect.bottom", {"start": v(-287.5, 212.5) * mm, "end": v(-212.5, 212.5) * mm, "construction": true});
            skLineSegment(sketch, "E179.rect.top", {"start": v(-287.5, 287.5) * mm, "end": v(-212.5, 287.5) * mm, "construction": true});
            skLineSegment(sketch, "E179.rect.left", {"start": v(-287.5, 212.5) * mm, "end": v(-287.5, 287.5) * mm, "construction": true});
            skLineSegment(sketch, "E179.rect.right", {"start": v(-212.5, 212.5) * mm, "end": v(-212.5, 287.5) * mm, "construction": true});
            skPoint(sketch, "E179.rect.middle", {"position": v(-250, 250) * mm});
            skCircle(sketch, "E180", {"center": v(-287.5, 287.5) * mm, "radius": 12.5 * mm});
            skCircle(sketch, "E181", {"center": v(-212.5, 287.5) * mm, "radius": 12.5 * mm});
            skCircle(sketch, "E182", {"center": v(-287.5, 212.5) * mm, "radius": 12.5 * mm});
            skCircle(sketch, "E183", {"center": v(-212.5, 212.5) * mm, "radius": 12.5 * mm});
            skLineSegment(sketch, "E184.MirrorCS", {"start": v(287.5, 287.5) * mm, "end": v(212.5, 287.5) * mm, "construction": true});
            skCircle(sketch, "E185.MirrorC", {"center": v(212.5, 287.5) * mm, "radius": 12.5 * mm});
            skCircle(sketch, "E186.MirrorC", {"center": v(287.5, 287.5) * mm, "radius": 12.5 * mm});
            skPoint(sketch, "E187.MirrorP", {"position": v(250, 250) * mm});
            skLineSegment(sketch, "E188.MirrorCS", {"start": v(287.5, 212.5) * mm, "end": v(287.5, 287.5) * mm, "construction": true});
            skLineSegment(sketch, "E189.MirrorCS", {"start": v(212.5, 212.5) * mm, "end": v(212.5, 287.5) * mm, "construction": true});
            skLineSegment(sketch, "E190.MirrorCS", {"start": v(287.5, 212.5) * mm, "end": v(212.5, 212.5) * mm, "construction": true});
            skCircle(sketch, "E191.MirrorC", {"center": v(212.5, 212.5) * mm, "radius": 12.5 * mm});
            skCircle(sketch, "E192.MirrorC", {"center": v(287.5, 212.5) * mm, "radius": 12.5 * mm});
            skCircle(sketch, "E193.MirrorC", {"center": v(287.5, -287.5) * mm, "radius": 12.5 * mm});
            skCircle(sketch, "E194.MirrorC", {"center": v(212.5, -287.5) * mm, "radius": 12.5 * mm});
            skCircle(sketch, "E195.MirrorC", {"center": v(-212.5, -287.5) * mm, "radius": 12.5 * mm});
            skCircle(sketch, "E196.MirrorC", {"center": v(-287.5, -287.5) * mm, "radius": 12.5 * mm});
            skCircle(sketch, "E197.MirrorC", {"center": v(287.5, -212.5) * mm, "radius": 12.5 * mm});
            skCircle(sketch, "E198.MirrorC", {"center": v(212.5, -212.5) * mm, "radius": 12.5 * mm});
            skCircle(sketch, "E199.MirrorC", {"center": v(-212.5, -212.5) * mm, "radius": 12.5 * mm});
            skCircle(sketch, "E200.MirrorC", {"center": v(-287.5, -212.5) * mm, "radius": 12.5 * mm});
            skLineSegment(sketch, "E201.MirrorCS", {"start": v(287.5, -287.5) * mm, "end": v(212.5, -287.5) * mm, "construction": true});
            skLineSegment(sketch, "E202.MirrorCS", {"start": v(-287.5, -287.5) * mm, "end": v(-212.5, -287.5) * mm, "construction": true});
            skLineSegment(sketch, "E203.MirrorCS", {"start": v(-250, -250) * mm, "end": v(250, -250) * mm});
            skLineSegment(sketch, "E204.MirrorCS", {"start": v(287.5, -212.5) * mm, "end": v(287.5, -287.5) * mm, "construction": true});
            skLineSegment(sketch, "E205.MirrorCS", {"start": v(212.5, -212.5) * mm, "end": v(212.5, -287.5) * mm, "construction": true});
            skLineSegment(sketch, "E206.MirrorCS", {"start": v(-212.5, -212.5) * mm, "end": v(-212.5, -287.5) * mm, "construction": true});
            skLineSegment(sketch, "E207.MirrorCS", {"start": v(-287.5, -212.5) * mm, "end": v(-287.5, -287.5) * mm, "construction": true});
            skPoint(sketch, "E208.MirrorP", {"position": v(250, -250) * mm});
            skPoint(sketch, "E209.MirrorP", {"position": v(-250, -250) * mm});
            skLineSegment(sketch, "E210.MirrorCS", {"start": v(287.5, -212.5) * mm, "end": v(212.5, -212.5) * mm, "construction": true});
            skLineSegment(sketch, "E211.MirrorCS", {"start": v(-287.5, -212.5) * mm, "end": v(-212.5, -212.5) * mm, "construction": true});
            skSolve(sketch);
        }
        {
            var Q0;
            Q0=qSketchRegion(id+"F15",true);
            var Q1;
            Q1=makeQuery(id+"F11.opExtrude","CAP_FACE",FACE,{"disambiguationData":[OSD([sQuery(id+"F10.wireOp",EDGE,"E173.rect.bottom"),sQuery(id+"F10.wireOp",EDGE,"E173.rect.top"),sQuery(id+"F10.wireOp",EDGE,"E173.rect.left"),sQuery(id+"F10.wireOp",EDGE,"E173.rect.right")])],"isStart":true});
            extrude(context, id + "F16", {"entities" : qUnion([Q0]), "operationType" : NewBodyOperationType.REMOVE, "endBound" : BoundingType.UP_TO_SURFACE, "oppositeDirection" : true, "endBoundEntityFace" : qUnion([Q1]), "depth" : mm});
        }
    });
